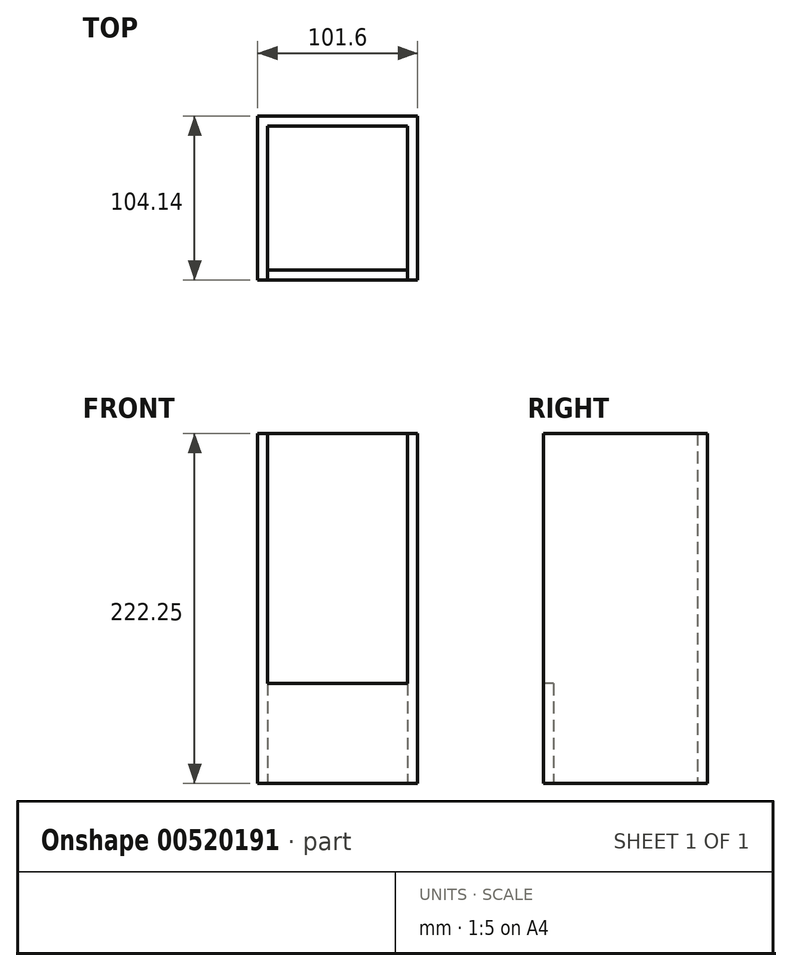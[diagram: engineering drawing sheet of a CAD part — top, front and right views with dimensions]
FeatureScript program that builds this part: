
annotation { "Feature Type Name" : "Feature", "Feature Type Description" : "" }
export const myFeature = defineFeature(function(context is Context, id is Id, definition is map)
    precondition{}
    {
        {
            var Q0;
            Q0=qCreatedBy(makeId("Top.planeOp"),FACE);
            var sketch = newSketch(context, id + "F0", { "sketchPlane" : qUnion([Q0])});
            skLineSegment(sketch, "E0.bottom", {"start": v(-46.23, 57.66) * mm, "end": v(42.67, 57.66) * mm});
            skLineSegment(sketch, "E0.top", {"start": v(-46.23, -33.78) * mm, "end": v(42.67, -33.78) * mm});
            skLineSegment(sketch, "E0.left", {"start": v(-46.23, 57.66) * mm, "end": v(-46.23, -33.78) * mm});
            skLineSegment(sketch, "E0.right", {"start": v(42.67, 57.66) * mm, "end": v(42.67, -33.78) * mm});
            skLineSegment(sketch, "E1.0", {"start": v(49.02, 64.01) * mm, "end": v(49.02, -40.13) * mm});
            skLineSegment(sketch, "E1.1", {"start": v(-52.58, 64.01) * mm, "end": v(49.02, 64.01) * mm});
            skLineSegment(sketch, "E1.2", {"start": v(-52.58, 64.01) * mm, "end": v(-52.58, -40.13) * mm});
            skLineSegment(sketch, "E1.3", {"start": v(-52.58, -40.13) * mm, "end": v(49.02, -40.13) * mm});
            skLineSegment(sketch, "E2", {"start": v(-46.23, -33.78) * mm, "end": v(-46.23, -40.13) * mm});
            skLineSegment(sketch, "E3", {"start": v(-46.23, -40.13) * mm, "end": v(42.67, -40.13) * mm});
            skLineSegment(sketch, "E4", {"start": v(42.67, -40.13) * mm, "end": v(42.67, -33.78) * mm});
            skSolve(sketch);
        }
        {
            var Q0;
            Q0=makeQuery(id+"F0.imprint","IMPRINT",FACE,{"disambiguationData":[TD([[makeQuery(id+"F0.imprint","IMPRINT",EDGE,{"derivedFrom":sQuery(id+"F0.wireOp",EDGE,"E0.top")}),-1.0]])]});
            extrude(context, id + "F1", {"entities" : qUnion([Q0]), "depth" : 63.5 * mm, "offsetDistance" : 25.4 * mm});
        }
        {
            var Q0;
            Q0=makeQuery(id+"F0.imprint","IMPRINT",FACE,{"disambiguationData":[TD([[makeQuery(id+"F0.imprint","IMPRINT",EDGE,{"derivedFrom":sQuery(id+"F0.wireOp",EDGE,"E0.bottom")}),1.0]])]});
            extrude(context, id + "F2", {"entities" : qUnion([Q0]), "operationType" : NewBodyOperationType.ADD, "depth" : 222.25 * mm, "offsetDistance" : 25.4 * mm});
        }
    });
